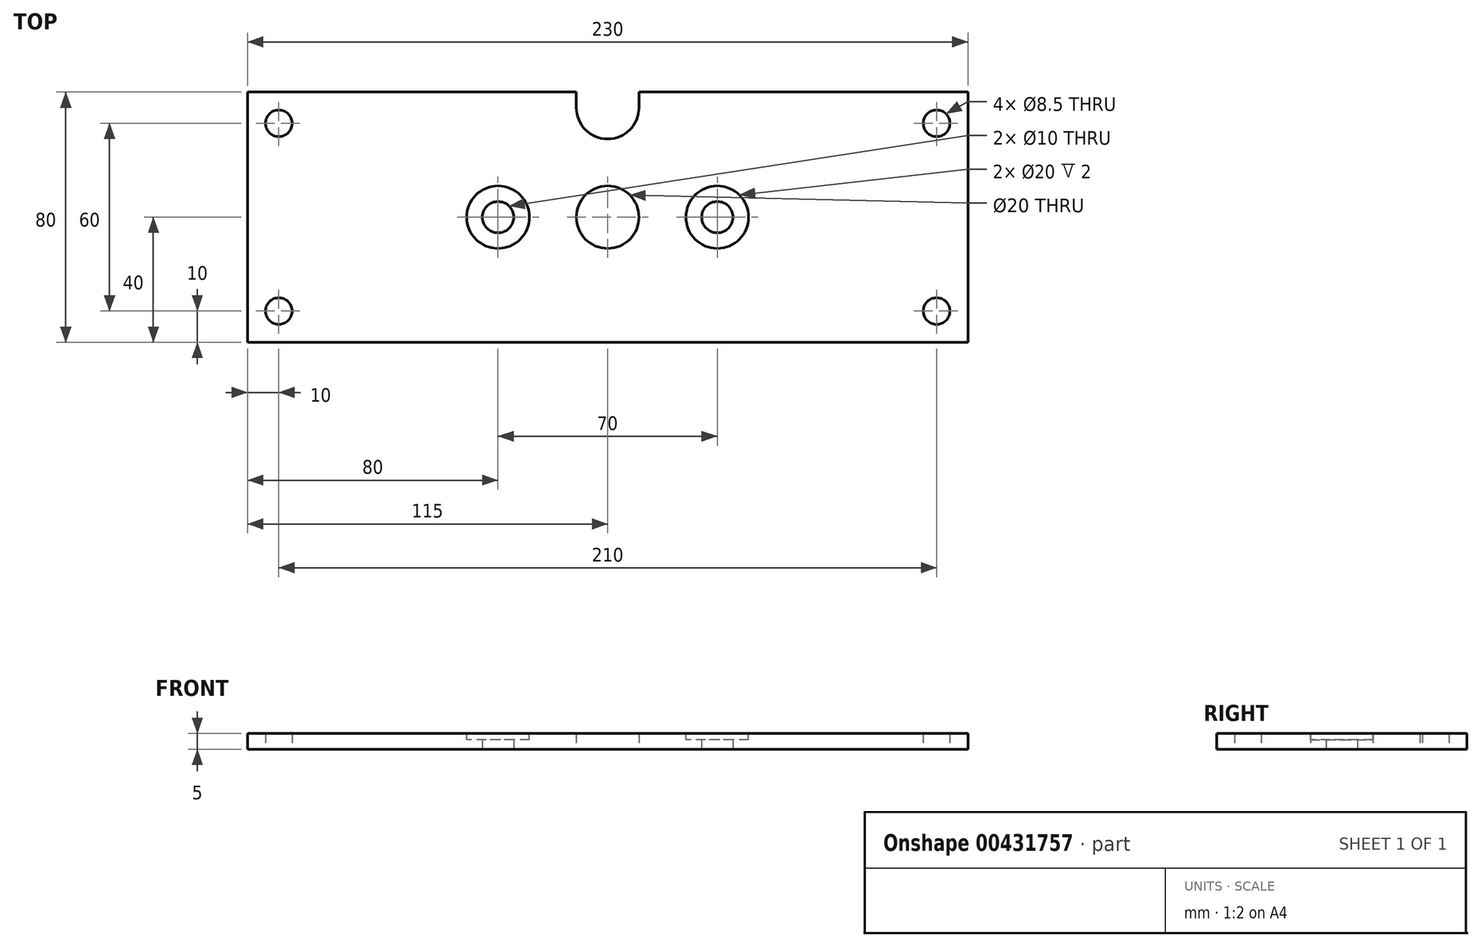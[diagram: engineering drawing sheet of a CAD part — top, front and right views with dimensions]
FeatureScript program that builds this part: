
annotation { "Feature Type Name" : "Feature", "Feature Type Description" : "" }
export const myFeature = defineFeature(function(context is Context, id is Id, definition is map)
    precondition{}
    {
        {
            var Q0;
            Q0=qCreatedBy(makeId("Top.planeOp"),FACE);
            var sketch = newSketch(context, id + "F0", { "sketchPlane" : qUnion([Q0])});
            skLineSegment(sketch, "E0.bottom", {"start": v(-115, 40) * mm, "end": v(115, 40) * mm});
            skLineSegment(sketch, "E0.top", {"start": v(-115, -40) * mm, "end": v(115, -40) * mm});
            skLineSegment(sketch, "E0.left", {"start": v(-115, 40) * mm, "end": v(-115, -40) * mm});
            skLineSegment(sketch, "E0.right", {"start": v(115, 40) * mm, "end": v(115, -40) * mm});
            skPoint(sketch, "E0.middle", {"position": v(0, 0) * mm});
            skCircle(sketch, "E1", {"center": v(0, 0) * mm, "radius": 10 * mm});
            skCircle(sketch, "E2", {"center": v(-105, 30) * mm, "radius": 4.25 * mm});
            skCircle(sketch, "E3", {"center": v(-35, 0) * mm, "radius": 5 * mm});
            skCircle(sketch, "E4", {"center": v(35, 0) * mm, "radius": 5 * mm});
            skLineSegment(sketch, "E5", {"start": v(-12.45, 35) * mm, "end": v(26.29, 35) * mm, "construction": true});
            skArc(sketch, "E6", {"start": v(10, 35) * mm, "mid": v(0, 25) * mm, "end": v(-10, 35) * mm});
            skLineSegment(sketch, "E7", {"start": v(-10, 35) * mm, "end": v(-10, 40) * mm});
            skLineSegment(sketch, "E8", {"start": v(10, 35) * mm, "end": v(10, 40) * mm});
            skLineSegment(sketch, "E9", {"start": v(10, 40) * mm, "end": v(-10, 40) * mm});
            skCircle(sketch, "E10", {"center": v(105, 30) * mm, "radius": 4.25 * mm});
            skCircle(sketch, "E11.MirrorC", {"center": v(-105, -30) * mm, "radius": 4.25 * mm});
            skCircle(sketch, "E12.MirrorC", {"center": v(105, -30) * mm, "radius": 4.25 * mm});
            skSolve(sketch);
        }
        {
            var Q0;
            Q0=makeQuery(id+"F0.imprint","IMPRINT",FACE,{"disambiguationData":[TD([[makeQuery(id+"F0.imprint","IMPRINT",EDGE,{"derivedFrom":sQuery(id+"F0.wireOp",EDGE,"E0.top")}),1.0]])]});
            extrude(context, id + "F1", {"entities" : qUnion([Q0]), "depth" : 5 * mm});
        }
        {
            var Q0;
            Q0=makeQuery(id+"F1.opExtrude","CAP_FACE",FACE,{"disambiguationData":[OSD([sQuery(id+"F0.wireOp",EDGE,"E0.bottom"),sQuery(id+"F0.wireOp",EDGE,"E0.top"),sQuery(id+"F0.wireOp",EDGE,"E0.left"),sQuery(id+"F0.wireOp",EDGE,"E0.right"),sQuery(id+"F0.wireOp",EDGE,"E1"),sQuery(id+"F0.wireOp",EDGE,"E2"),sQuery(id+"F0.wireOp",EDGE,"E3"),sQuery(id+"F0.wireOp",EDGE,"E4"),sQuery(id+"F0.wireOp",EDGE,"E6"),sQuery(id+"F0.wireOp",EDGE,"E7"),sQuery(id+"F0.wireOp",EDGE,"E8"),sQuery(id+"F0.wireOp",EDGE,"E10")])],"isStart":false});
            var sketch = newSketch(context, id + "F2", { "sketchPlane" : qUnion([Q0])});
            skCircle(sketch, "E13", {"center": v(-35, 0) * mm, "radius": 10 * mm});
            skCircle(sketch, "E14", {"center": v(35, 0) * mm, "radius": 10 * mm});
            skSolve(sketch);
        }
        {
            var Q0;
            Q0=makeQuery(id+"F2.imprint","IMPRINT",FACE,{"disambiguationData":[TD([[makeQuery(id+"F2.imprint","IMPRINT",EDGE,{"derivedFrom":makeQuery(id+"F1.opExtrude","CAP_EDGE",EDGE,{"disambiguationData":[OSD([sQuery(id+"F0.wireOp",EDGE,"E3")])],"isStart":false})}),1.0]])]});
            var Q1;
            Q1=makeQuery(id+"F2.imprint","IMPRINT",FACE,{"disambiguationData":[TD([[makeQuery(id+"F2.imprint","IMPRINT",EDGE,{"derivedFrom":makeQuery(id+"F1.opExtrude","CAP_EDGE",EDGE,{"disambiguationData":[OSD([sQuery(id+"F0.wireOp",EDGE,"E4")])],"isStart":false})}),1.0]])]});
            var Q2;
            Q2=makeQuery(id+"F2.imprint","IMPRINT",FACE,{"disambiguationData":[TD([[makeQuery(id+"F2.imprint","IMPRINT",EDGE,{"derivedFrom":sQuery(id+"F2.wireOp",EDGE,"E14")}),1.0]])]});
            var Q3;
            Q3=makeQuery(id+"F2.imprint","IMPRINT",FACE,{"disambiguationData":[TD([[makeQuery(id+"F2.imprint","IMPRINT",EDGE,{"derivedFrom":sQuery(id+"F2.wireOp",EDGE,"E13")}),1.0]])]});
            extrude(context, id + "F3", {"entities" : qUnion([Q0, Q1, Q2, Q3]), "operationType" : NewBodyOperationType.REMOVE, "oppositeDirection" : true, "depth" : 2 * mm});
        }
    });
